# Revit family: BSC-Class-II_Type-B1_NuAire_Labgard_430-435
name_source: partatom
category: Mechanical Equipment
units: mm (PartAtom-declared; Revit-internal decimal feet)

## family parameters
Always vertical = Yes
Classification Number = 23.40.70.11.11.11.11
Cut with Voids When Loaded = No
Maintain Annotation Orientation = No
Part Type = Normal
Room Calculation Point = No
Round Connector Dimension = Use Radius
Shared = No
Work Plane-Based = No

## types (8) — shared parameters
Assembly Code = E1020720
Construction Details = http://www.arcat.com
DEPTH = 2' - 4"
Default Elevation = 0' - 0"
Description = Class II Type B2 Biological Safety Cabinet
EXHAUST HEIGHT = 1' - 1"
EXHAUST RING = 0' - 6"
EXHAUST RING BACK = 1' - 0"
EXHAUST RING SIDE = 1' - 6 3/8"
Exhaust Flow = 647 CFM
INTAKE RING BACK = 1' - 0"
INTAKE RING SIDE = 1' - 3 1/2"
Keynote = 11 53 00
Manufacturer = Nuaire Inc
Manufacturer Fax = 763-553-0459
Manufacturer Website = http://www.nuaire.com
Plumbing = 0' - 0 3/16"
Plumbing Height = 0' - 3"
Product Data = http://www.arcat.com
Product Properties = http://www.nuaire.com
Revision = R1_12/2015
Room Inflow = 647 CFM
Sales Information = http://www.nuaire.com
Specification = http://www.arcat.com
Type Comments = Contact Sales for Info: 800-328-3352, 888-4-NUAIRE, www.nuaire.com
URL = http://www.nuaire.com
WIDTH = 6' - 5 5/8"
WORK SURFACE HEIGHT = 2' - 8 1/2"
control panel = 2' - 6 13/16"

## per-type parameters (varying)
| type | Model |
| NU430-600 - 36 WORK SURFACE HEIGHT | NU-430-600 |
| NU430-400 - 30 WORK SURFACE HEIGHT | NU-430-400 |
| NU430-400 - 36 WORK SURFACE HEIGHT | NU-430-400 |
| NU430-600 - 30 WORK SURFACE HEIGHT | NU-430-600 |
| NU435-600 - 36 WORK SURFACE HEIGHT | NU-435-600 |
| NU435-400 - 30 WORK SURFACE HEIGHT | NU-435-400 |
| NU435-400 - 36 WORK SURFACE HEIGHT | NU-435-400 |
| NU435-600 - 30 WORK SURFACE HEIGHT | NU-435-600 |

## geometry (parser evidence)
native form markers: Blend x10, Sweep x3
no freeform markers — native parametric forms only
